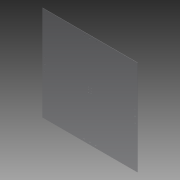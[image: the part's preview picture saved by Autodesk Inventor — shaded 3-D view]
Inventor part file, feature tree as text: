
AUTODESK INVENTOR PART (.ipt)
format: ipt  version: 2014 (Build 180170000, 170)  size: 114,688 bytes
history: native  units: in
note: dims shown in document units (in); Inventor stores cm internally (conversion verified against a paired STEP export)
features: extrude x1, sketch x1
ambient origin geometry x8: Origin, YZ Plane, XZ Plane, XY Plane, X Axis, Y Axis, Z Axis, Center Point
bodies: Solid1 (feature_tree)
feature tree (2):
  extrude  "Extrusion1"  Depth=20.0in
  sketch  "Sketch1"  dims[d0=20.0in d1=20.0in d16=0.0625in d17=0.0in d18=1.0in d19=1.5in d20=0.196in d21=0.25in d22=0.25in d23=0.7874in d25=0.5in d26=1.1811in d28=0.5in d31=0.75in d32=3.0in d33=0.196in d34=0.25in d35=0.25in d36=0.25in d37=1.5748in d39=360.0deg]
